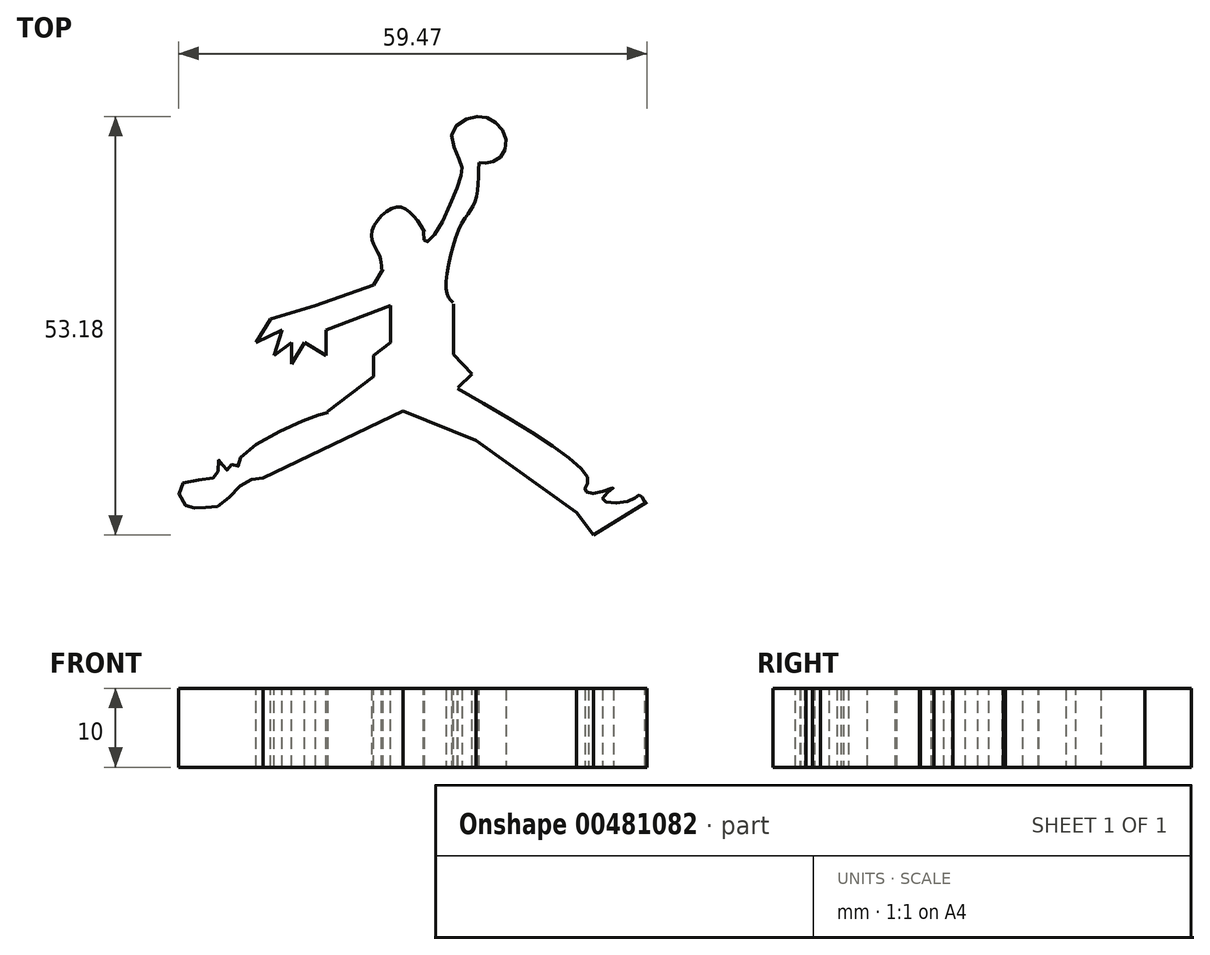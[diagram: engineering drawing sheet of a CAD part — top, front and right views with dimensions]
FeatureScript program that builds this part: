
annotation { "Feature Type Name" : "Feature", "Feature Type Description" : "" }
export const myFeature = defineFeature(function(context is Context, id is Id, definition is map)
    precondition{}
    {
        {
            var Q0;
            Q0=qCreatedBy(makeId("Top.planeOp"),FACE);
            var sketch = newSketch(context, id + "F0", { "sketchPlane" : qUnion([Q0])});
            skFitSpline(sketch, "E0", {"points": [v(4.6, 2.07) * mm, v(3.77, 3.6) * mm, v(5.6, 11.9) * mm, v(7.35, 14.73) * mm, v(7.89, 19.84) * mm], "startDerivative": vector(-6.9, 6.47) * mm, "endDerivative": vector(0.25, 21.46) * mm});
            skFitSpline(sketch, "E1", {"points": [v(7.89, 19.84) * mm, v(9.22, 19.84) * mm, v(10.82, 20.79) * mm, v(11.25, 23.07) * mm, v(9.55, 25.27) * mm, v(7.01, 25.61) * mm, v(4.47, 23.58) * mm, v(5.6, 19.84) * mm, v(5.6, 18.08) * mm, v(2.53, 11.13) * mm, v(1.09, 9.78) * mm, v(0.83, 11.05) * mm], "startDerivative": vector(19.66, -2.16) * mm, "endDerivative": vector(-0.92, 26.85) * mm});
            skSolve(sketch);
        }
        {
            var Q0;
            Q0=qCreatedBy(makeId("Top.planeOp"),FACE);
            var sketch = newSketch(context, id + "F1", { "sketchPlane" : qUnion([Q0])});
            skFitSpline(sketch, "E2", {"points": [v(-11.28, -11.87) * mm, v(-13.92, -12.72) * mm, v(-22.45, -17.76) * mm, v(-22.76, -18.77) * mm, v(-23.77, -18.54) * mm, v(-24.23, -19.31) * mm, v(-25.09, -17.84) * mm, v(-25.24, -19.31) * mm, v(-26.17, -20.32) * mm, v(-30.05, -21.17) * mm, v(-29.35, -23.73) * mm, v(-27.64, -23.96) * mm, v(-25.16, -23.73) * mm, v(-21.98, -20.86) * mm, v(-19.5, -20.24) * mm], "startDerivative": vector(-25.08, -6.14) * mm, "endDerivative": vector(33.87, 1.28) * mm});
            skLineSegment(sketch, "E3", {"start": v(-19.5, -20.24) * mm, "end": v(-1.75, -11.71) * mm});
            skLineSegment(sketch, "E4", {"start": v(-1.75, -11.71) * mm, "end": v(7.5, -15.45) * mm});
            skLineSegment(sketch, "E5", {"start": v(7.5, -15.45) * mm, "end": v(20.29, -24.58) * mm});
            skLineSegment(sketch, "E6", {"start": v(20.29, -24.58) * mm, "end": v(22.43, -27.45) * mm});
            skLineSegment(sketch, "E7", {"start": v(22.43, -27.45) * mm, "end": v(29.23, -23.27) * mm});
            skSolve(sketch);
        }
        {
            var Q0;
            Q0=qCreatedBy(makeId("Top.planeOp"),FACE);
            var sketch = newSketch(context, id + "F2", { "sketchPlane" : qUnion([Q0])});
            skFitSpline(sketch, "E8", {"points": [v(28.97, -23.33) * mm, v(28.32, -22.4) * mm, v(27.01, -23.11) * mm, v(23.6, -22.9) * mm, v(24.98, -21.45) * mm, v(22.66, -22.17) * mm, v(21.36, -21.67) * mm, v(21.8, -20.5) * mm, v(5.2, -8.84) * mm], "startDerivative": vector(-8.26, 17.55) * mm, "endDerivative": vector(-76.33, 44.45) * mm});
            skSolve(sketch);
        }
        {
            var Q0;
            Q0=qCreatedBy(makeId("Top.planeOp"),FACE);
            var sketch = newSketch(context, id + "F3", { "sketchPlane" : qUnion([Q0])});
            skLineSegment(sketch, "E9", {"start": v(5.26, -8.72) * mm, "end": v(7.04, -7.01) * mm});
            skLineSegment(sketch, "E10", {"start": v(7.04, -7.01) * mm, "end": v(4.7, -4.55) * mm});
            skLineSegment(sketch, "E11", {"start": v(4.7, -4.55) * mm, "end": v(4.7, 1.86) * mm});
            skSolve(sketch);
        }
        {
            var Q0;
            Q0=qCreatedBy(makeId("Top.planeOp"),FACE);
            var sketch = newSketch(context, id + "F4", { "sketchPlane" : qUnion([Q0])});
            skLineSegment(sketch, "E12", {"start": v(-11.3, -11.74) * mm, "end": v(-5.5, -7.32) * mm});
            skLineSegment(sketch, "E13", {"start": v(-5.5, -7.32) * mm, "end": v(-5.5, -4.68) * mm});
            skLineSegment(sketch, "E14", {"start": v(-5.5, -4.68) * mm, "end": v(-3.31, -3.01) * mm});
            skLineSegment(sketch, "E15", {"start": v(-3.31, -3.01) * mm, "end": v(-3.31, 1.73) * mm});
            skLineSegment(sketch, "E16", {"start": v(-3.31, 1.73) * mm, "end": v(-11.54, -1.4) * mm});
            skLineSegment(sketch, "E17", {"start": v(-11.54, -1.4) * mm, "end": v(-11.54, -4.68) * mm});
            skLineSegment(sketch, "E18", {"start": v(-11.54, -4.68) * mm, "end": v(-14.25, -3.01) * mm});
            skLineSegment(sketch, "E19", {"start": v(-14.25, -3.01) * mm, "end": v(-15.9, -5.7) * mm});
            skLineSegment(sketch, "E20", {"start": v(-15.9, -5.7) * mm, "end": v(-15.9, -3.01) * mm});
            skLineSegment(sketch, "E21", {"start": v(-15.9, -3.01) * mm, "end": v(-18.1, -4.68) * mm});
            skLineSegment(sketch, "E22", {"start": v(-18.1, -4.68) * mm, "end": v(-17.1, -1.4) * mm});
            skLineSegment(sketch, "E23", {"start": v(-17.1, -1.4) * mm, "end": v(-20.43, -3.01) * mm});
            skLineSegment(sketch, "E24", {"start": v(-20.43, -3.01) * mm, "end": v(-18.57, 0) * mm});
            skLineSegment(sketch, "E25", {"start": v(-18.57, 0) * mm, "end": v(-12.83, 1.73) * mm});
            skLineSegment(sketch, "E26", {"start": v(-12.83, 1.73) * mm, "end": v(-5.5, 4.29) * mm});
            skLineSegment(sketch, "E27", {"start": v(-5.5, 4.29) * mm, "end": v(-4.25, 6.32) * mm});
            skSolve(sketch);
        }
        {
            var Q0;
            Q0=qCreatedBy(makeId("Top.planeOp"),FACE);
            var sketch = newSketch(context, id + "F5", { "sketchPlane" : qUnion([Q0])});
            skFitSpline(sketch, "E28", {"points": [v(-4.48, 6.32) * mm, v(-4.8, 8.18) * mm, v(-5.73, 10.94) * mm, v(-2.4, 14.22) * mm, v(1, 11.05) * mm], "startDerivative": vector(-0.33, 9.86) * mm, "endDerivative": vector(10.47, -16.76) * mm});
            skSolve(sketch);
        }
        {
            var Q0;
            Q0=sQuery(id+"F4.wireOp",EDGE,"E15");
            var Q1;
            Q1=sQuery(id+"F4.wireOp",EDGE,"E27");
            var Q2;
            Q2=sQuery(id+"F5.wireOp",EDGE,"E28");
            var Q3;
            Q3=sQuery(id+"F3.wireOp",EDGE,"E10");
            var Q4;
            Q4=sQuery(id+"F1.wireOp",EDGE,"E4");
            var Q5;
            Q5=sQuery(id+"F3.wireOp",EDGE,"E11");
            var Q6;
            Q6=sQuery(id+"F4.wireOp",EDGE,"E13");
            var Q7;
            Q7=sQuery(id+"F4.wireOp",EDGE,"E14");
            var Q8;
            Q8=sQuery(id+"F3.wireOp",EDGE,"E9");
            var Q9;
            Q9=sQuery(id+"F4.wireOp",EDGE,"E17");
            var Q10;
            Q10=sQuery(id+"F4.wireOp",EDGE,"E20");
            var Q11;
            Q11=sQuery(id+"F4.wireOp",EDGE,"E26");
            var Q12;
            Q12=sQuery(id+"F4.wireOp",EDGE,"E22");
            var Q13;
            Q13=sQuery(id+"F4.wireOp",EDGE,"E24");
            var Q14;
            Q14=sQuery(id+"F4.wireOp",EDGE,"E12");
            var Q15;
            Q15=sQuery(id+"F4.wireOp",EDGE,"E23");
            var Q16;
            Q16=sQuery(id+"F4.wireOp",EDGE,"E25");
            var Q17;
            Q17=sQuery(id+"F4.wireOp",EDGE,"E19");
            var Q18;
            Q18=sQuery(id+"F1.wireOp",EDGE,"E3");
            var Q19;
            Q19=sQuery(id+"F4.wireOp",EDGE,"E18");
            var Q20;
            Q20=sQuery(id+"F4.wireOp",EDGE,"E16");
            var Q21;
            Q21=sQuery(id+"F4.wireOp",EDGE,"E21");
            var Q22;
            Q22=sQuery(id+"F1.wireOp",EDGE,"E2");
            var Q23;
            Q23=sQuery(id+"F2.wireOp",EDGE,"E8");
            var Q24;
            Q24=sQuery(id+"F0.wireOp",EDGE,"E0");
            var Q25;
            Q25=sQuery(id+"F1.wireOp",EDGE,"E6");
            var Q26;
            Q26=sQuery(id+"F1.wireOp",EDGE,"E5");
            var Q27;
            Q27=sQuery(id+"F1.wireOp",EDGE,"E7");
            var Q28;
            Q28=sQuery(id+"F0.wireOp",EDGE,"E1");
            extrude(context, id + "F6", {"bodyType" : ToolBodyType.SURFACE, "surfaceEntities" : qUnion([Q0, Q1, Q2, Q3, Q4, Q5, Q6, Q7, Q8, Q9, Q10, Q11, Q12, Q13, Q14, Q15, Q16, Q17, Q18, Q19, Q20, Q21, Q22, Q23, Q24, Q25, Q26, Q27, Q28]), "depth" : 10 * mm});
        }
    });
